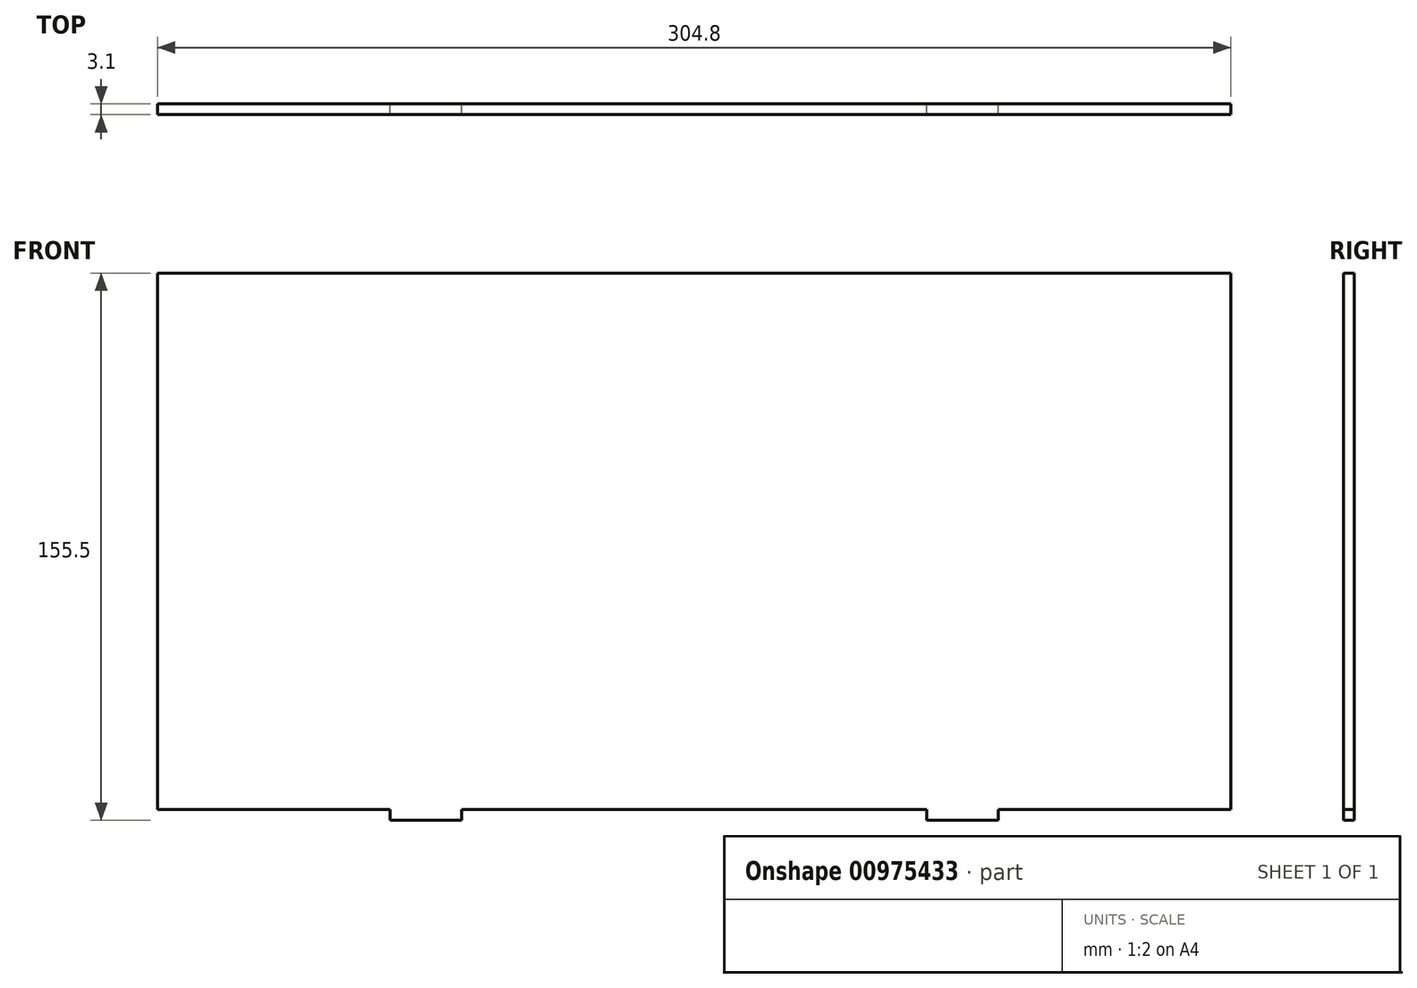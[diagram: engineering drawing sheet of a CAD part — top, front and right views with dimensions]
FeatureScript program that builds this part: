
annotation { "Feature Type Name" : "Feature", "Feature Type Description" : "" }
export const myFeature = defineFeature(function(context is Context, id is Id, definition is map)
    precondition{}
    {
        {
            var Q0;
            Q0=qCreatedBy(makeId("Front.planeOp"),FACE);
            var sketch = newSketch(context, id + "F0", { "sketchPlane" : qUnion([Q0])});
            skLineSegment(sketch, "E0.bottom", {"start": v(0, 0) * mm, "end": v(304.8, 0) * mm});
            skLineSegment(sketch, "E0.top", {"start": v(0, 152.4) * mm, "end": v(304.8, 152.4) * mm});
            skLineSegment(sketch, "E0.left", {"start": v(0, 0) * mm, "end": v(0, 152.4) * mm});
            skLineSegment(sketch, "E0.right", {"start": v(304.8, 0) * mm, "end": v(304.8, 152.4) * mm});
            skLineSegment(sketch, "E1", {"start": v(152.4, 152.4) * mm, "end": v(152.4, 0) * mm, "construction": true});
            skArc(sketch, "E2", {"start": v(152.4, 0) * mm, "mid": v(107.76, 107.76) * mm, "end": v(0, 152.4) * mm});
            skLineSegment(sketch, "E3.top", {"start": v(304.8, 0) * mm, "end": v(301.7, 0) * mm});
            skLineSegment(sketch, "E3.left", {"start": v(304.8, 25.4) * mm, "end": v(304.8, 0) * mm});
            skLineSegment(sketch, "E4.bottom", {"start": v(66.04, 0) * mm, "end": v(86.36, 0) * mm});
            skLineSegment(sketch, "E4.top", {"start": v(66.04, -3.1) * mm, "end": v(86.36, -3.1) * mm});
            skLineSegment(sketch, "E4.left", {"start": v(66.04, 0) * mm, "end": v(66.04, -3.1) * mm});
            skLineSegment(sketch, "E4.right", {"start": v(86.36, 0) * mm, "end": v(86.36, -3.1) * mm});
            skLineSegment(sketch, "E5", {"start": v(76.2, 0) * mm, "end": v(76.2, 152.4) * mm, "construction": true});
            skLineSegment(sketch, "E6.MirrorCS", {"start": v(238.76, 0) * mm, "end": v(238.76, -3.1) * mm});
            skLineSegment(sketch, "E7.MirrorCS", {"start": v(238.76, -3.1) * mm, "end": v(218.44, -3.1) * mm});
            skLineSegment(sketch, "E8.MirrorCS", {"start": v(218.44, 0) * mm, "end": v(218.44, -3.1) * mm});
            skLineSegment(sketch, "E9", {"start": v(0, 0) * mm, "end": v(26.46, 150.08) * mm});
            skLineSegment(sketch, "E10.1.0", {"start": v(0, 0) * mm, "end": v(52.12, 143.2) * mm});
            skLineSegment(sketch, "E10.2.0", {"start": v(0, 0) * mm, "end": v(76.2, 131.98) * mm});
            skLineSegment(sketch, "E10.3.0", {"start": v(0, 0) * mm, "end": v(97.96, 116.75) * mm});
            skLineSegment(sketch, "E10.4.0", {"start": v(0, 0) * mm, "end": v(116.75, 97.96) * mm});
            skLineSegment(sketch, "E10.5.0", {"start": v(0, 0) * mm, "end": v(131.98, 76.2) * mm});
            skLineSegment(sketch, "E10.6.0", {"start": v(0, 0) * mm, "end": v(143.2, 52.12) * mm});
            skLineSegment(sketch, "E10.7.0", {"start": v(0, 0) * mm, "end": v(150.08, 26.46) * mm});
            skLineSegment(sketch, "E10.8.0", {"start": v(0, 0) * mm, "end": v(152.4, 0) * mm});
            skLineSegment(sketch, "E10.anchor1", {"start": v(0, 0) * mm, "end": v(26.46, 150.08) * mm, "construction": true});
            skLineSegment(sketch, "E10.anchor2", {"start": v(0, 0) * mm, "end": v(152.4, 0) * mm, "construction": true});
            skSolve(sketch);
        }
        {
            var Q0;
            Q0 = qSketchRegion(id + "F0", true);
            extrude(context, id + "F1", {"entities" : qUnion([Q0]), "depth" : 3.1 * mm, "offsetDistance" : 25.4 * mm});
        }
    });
